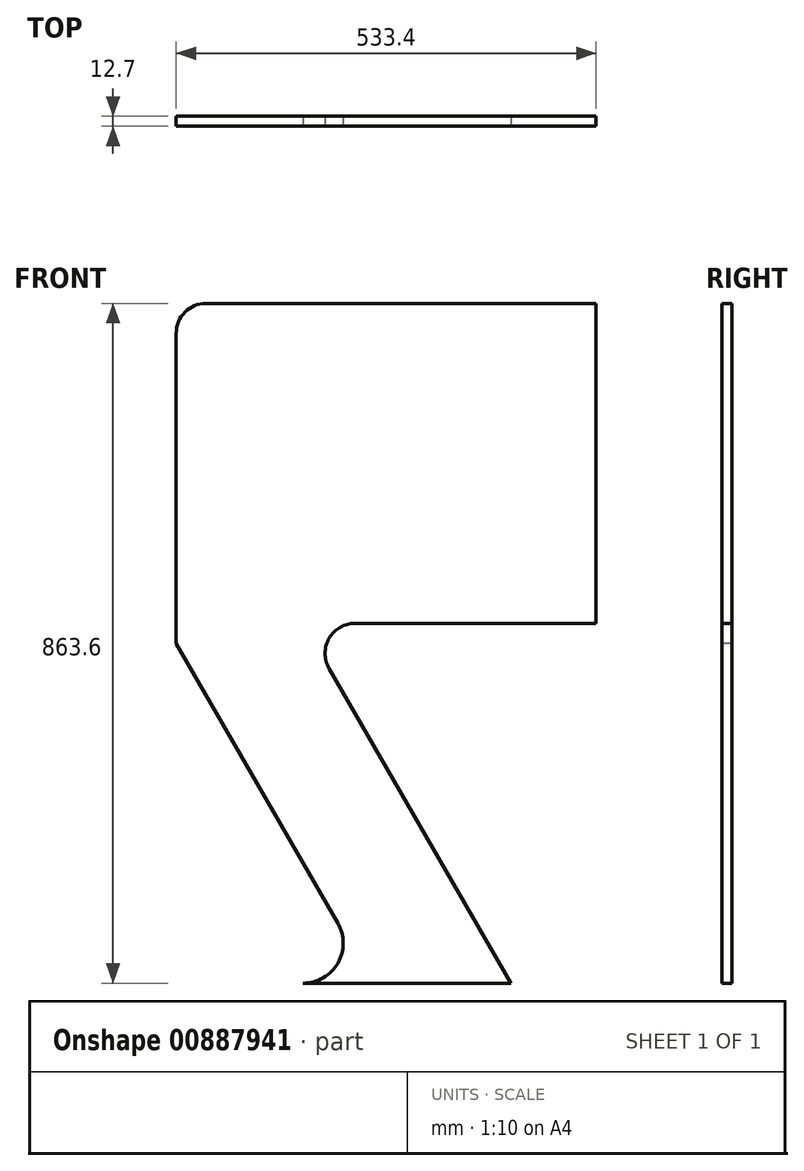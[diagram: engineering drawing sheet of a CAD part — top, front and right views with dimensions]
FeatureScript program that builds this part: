
annotation { "Feature Type Name" : "Feature", "Feature Type Description" : "" }
export const myFeature = defineFeature(function(context is Context, id is Id, definition is map)
    precondition{}
    {
        {
            var Q0;
            Q0=qCreatedBy(makeId("Front.planeOp"),FACE);
            var sketch = newSketch(context, id + "F0", { "sketchPlane" : qUnion([Q0])});
            skLineSegment(sketch, "E0.bottom", {"start": v(266.7, 431.8) * mm, "end": v(-266.7, 431.8) * mm});
            skLineSegment(sketch, "E0.top", {"start": v(266.7, -431.8) * mm, "end": v(-266.7, -431.8) * mm});
            skLineSegment(sketch, "E0.left", {"start": v(266.7, 431.8) * mm, "end": v(266.7, -431.8) * mm});
            skLineSegment(sketch, "E0.right", {"start": v(-266.7, 431.8) * mm, "end": v(-266.7, -431.8) * mm});
            skPoint(sketch, "E0.middle", {"position": v(0, 0) * mm});
            skSolve(sketch);
        }
        {
            var Q0;
            Q0=makeQuery(id+"F0.imprint","IMPRINT",FACE,{"disambiguationData":[TD([[makeQuery(id+"F0.imprint","IMPRINT",EDGE,{"derivedFrom":sQuery(id+"F0.wireOp",EDGE,"E0.bottom")}),1.0]])]});
            extrude(context, id + "F1", {"entities" : qUnion([Q0]), "depth" : 12.7 * mm, "offsetDistance" : 25.4 * mm});
        }
        {
            var Q0;
            Q0=makeQuery(id+"F1.opExtrude","CAP_FACE",FACE,{"disambiguationData":[OSD([sQuery(id+"F0.wireOp",EDGE,"E0.bottom"),sQuery(id+"F0.wireOp",EDGE,"E0.top"),sQuery(id+"F0.wireOp",EDGE,"E0.left"),sQuery(id+"F0.wireOp",EDGE,"E0.right")])],"isStart":false});
            var sketch = newSketch(context, id + "F2", { "sketchPlane" : qUnion([Q0])});
            skLineSegment(sketch, "E1", {"start": v(-266.7, 0) * mm, "end": v(-61.4, -355.6) * mm});
            skLineSegment(sketch, "E2", {"start": v(-105.39, 25.4) * mm, "end": v(266.7, 25.4) * mm});
            skLineSegment(sketch, "E3", {"start": v(266.7, 25.4) * mm, "end": v(266.7, 431.8) * mm});
            skLineSegment(sketch, "E4", {"start": v(-105.39, 25.4) * mm, "end": v(158.58, -431.8) * mm});
            skLineSegment(sketch, "E5", {"start": v(-61.4, -355.6) * mm, "end": v(70.59, -279.4) * mm, "construction": true});
            skArc(sketch, "E6", {"start": v(-105.39, -431.8) * mm, "mid": v(-61.4, -406.4) * mm, "end": v(-61.4, -355.6) * mm});
            skSolve(sketch);
        }
        {
            var Q0;
            Q0 = qSketchRegion(id + "F2", true);
            var Q1;
            {var subQ0=sQuery(id+"F2.wireOp",EDGE,"E1");Q1=makeQuery(id+"F2.imprint","IMPRINT",FACE,{"disambiguationData":[TD([[makeQuery(id+"F2.imprint","IMPRINT",EDGE,{"derivedFrom":subQ0}),-1.0]])]});}
            var Q2;
            {var subQ0=sQuery(id+"F2.wireOp",EDGE,"E2");Q2=makeQuery(id+"F2.imprint","IMPRINT",FACE,{"disambiguationData":[TD([[makeQuery(id+"F2.imprint","IMPRINT",EDGE,{"derivedFrom":subQ0}),-1.0]])]});}
            extrude(context, id + "F3", {"entities" : qUnion([Q0, Q1, Q2]), "operationType" : NewBodyOperationType.REMOVE, "endBound" : BoundingType.THROUGH_ALL, "oppositeDirection" : true, "depth" : 25.4 * mm, "offsetDistance" : 25.4 * mm});
        }
        {
            var Q0;
            {var subQ0=sQuery(id+"F0.wireOp",EDGE,"E0.right");var subQ1=sQuery(id+"F0.wireOp",EDGE,"E0.bottom");Q0=makeQuery(id+"F3.boolean.opBoolean","MERGE",EDGE,{"derivedFrom":[makeQuery(id+"F1.opExtrude","SWEPT_EDGE",EDGE,{"disambiguationData":[OSD([subQ1,subQ0])]})],"fromTools":[makeQuery(id+"F3.opExtrude","SWEPT_EDGE",EDGE,{"disambiguationData":[OSD([subQ1,subQ0,sQuery(id+"F2.wireOp",EDGE,"E1")])]})]});}
            var Q1;
            Q1=makeQuery(id+"F3.boolean.opBoolean","COPY",EDGE,{"derivedFrom":makeQuery(id+"F3.opExtrude","SWEPT_EDGE",EDGE,{"disambiguationData":[OSD([sQuery(id+"F2.wireOp",EDGE,"E2"),sQuery(id+"F2.wireOp",EDGE,"E4")])]})});
            fillet(context, id + "F4", {"entities" : qUnion([Q0, Q1]), "radius" : 38.1 * mm, "tangentPropagation" : true, "allowEdgeOverflow" : false});
        }
    });
